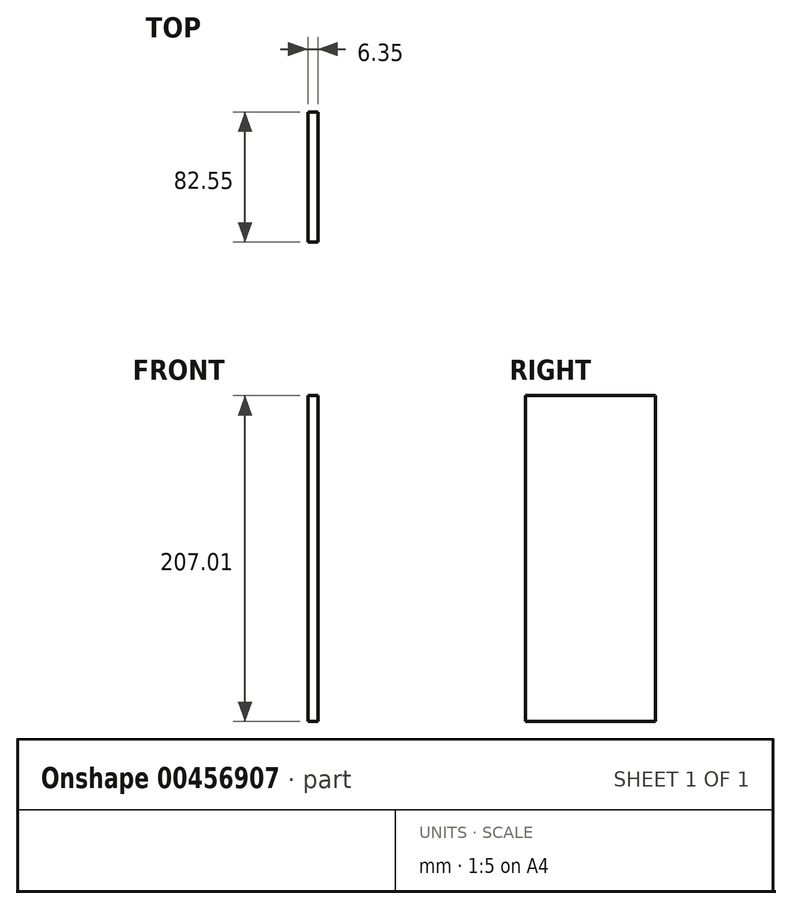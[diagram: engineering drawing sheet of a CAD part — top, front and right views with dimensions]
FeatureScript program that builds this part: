
annotation { "Feature Type Name" : "Feature", "Feature Type Description" : "" }
export const myFeature = defineFeature(function(context is Context, id is Id, definition is map)
    precondition{}
    {
        {
            var Q0;
            Q0=qCreatedBy(makeId("Right.planeOp"),FACE);
            var sketch = newSketch(context, id + "F0", { "sketchPlane" : qUnion([Q0])});
            skLineSegment(sketch, "E0.bottom", {"start": v(-94.16, 97.02) * mm, "end": v(-11.6, 97.02) * mm});
            skLineSegment(sketch, "E0.top", {"start": v(-94.16, -110) * mm, "end": v(-11.6, -110) * mm});
            skLineSegment(sketch, "E0.left", {"start": v(-94.16, 97.02) * mm, "end": v(-94.16, -110) * mm});
            skLineSegment(sketch, "E1", {"start": v(-11.6, -110) * mm, "end": v(-11.6, 97.02) * mm});
            skSolve(sketch);
        }
        {
            var Q0;
            Q0=makeQuery(id+"F0.imprint","IMPRINT",FACE,{"disambiguationData":[TD([[makeQuery(id+"F0.imprint","IMPRINT",EDGE,{"derivedFrom":sQuery(id+"F0.wireOp",EDGE,"E0.bottom")}),-1.0]])]});
            extrude(context, id + "F1", {"entities" : qUnion([Q0]), "depth" : 6.35 * mm});
        }
    });
